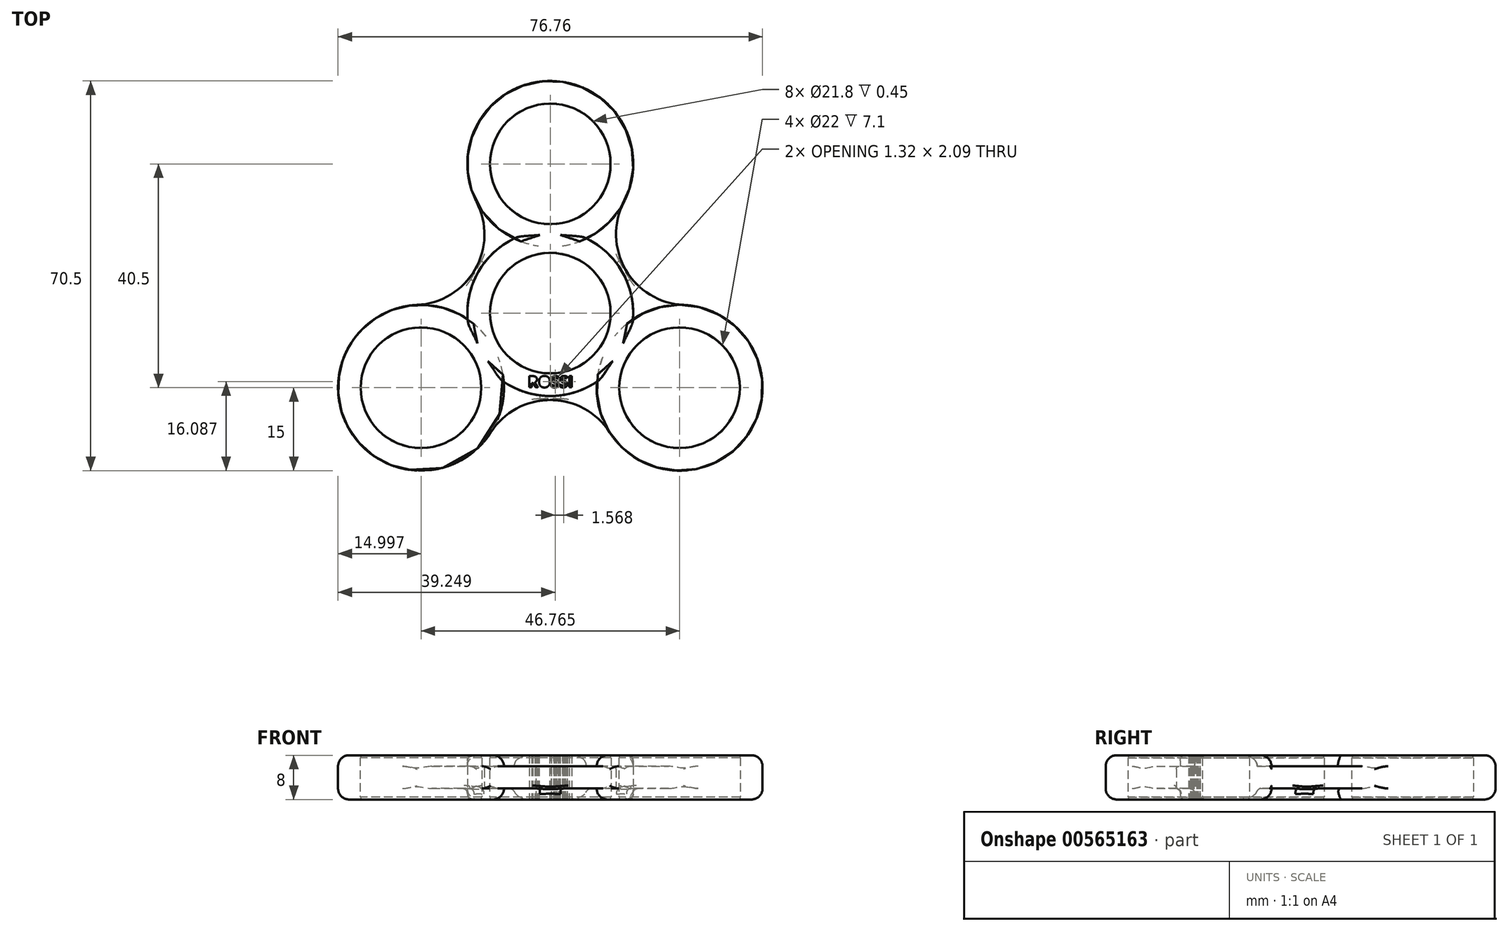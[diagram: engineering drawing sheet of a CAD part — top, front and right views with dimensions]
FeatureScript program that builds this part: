
annotation { "Feature Type Name" : "Feature", "Feature Type Description" : "" }
export const myFeature = defineFeature(function(context is Context, id is Id, definition is map)
    precondition{}
    {
        {
            var Q0;
            Q0=qCreatedBy(makeId("Top.planeOp"),FACE);
            var sketch = newSketch(context, id + "F0", { "sketchPlane" : qUnion([Q0])});
            skCircle(sketch, "E0", {"center": v(0, 0) * mm, "radius": 10.9 * mm});
            skCircle(sketch, "E1", {"center": v(0, 27) * mm, "radius": 10.9 * mm});
            skCircle(sketch, "E2.1.0", {"center": v(-23.38, -13.5) * mm, "radius": 10.9 * mm});
            skCircle(sketch, "E2.2.0", {"center": v(23.38, -13.5) * mm, "radius": 10.9 * mm});
            skArc(sketch, "E3", {"start": v(6.54, 13.5) * mm, "mid": v(0, 42) * mm, "end": v(-6.54, 13.5) * mm});
            skArc(sketch, "E4.1.0", {"start": v(8.42, -12.41) * mm, "mid": v(36.37, -21) * mm, "end": v(14.96, -1.09) * mm});
            skArc(sketch, "E4.2.0", {"start": v(-14.96, -1.09) * mm, "mid": v(-36.37, -21) * mm, "end": v(-8.42, -12.41) * mm});
            skArc(sketch, "E5", {"start": v(-8.42, -12.41) * mm, "mid": v(0, -15) * mm, "end": v(8.42, -12.41) * mm});
            skArc(sketch, "E6", {"start": v(-24.08, 1.48) * mm, "mid": v(-13.61, 7.86) * mm, "end": v(-13.33, 20.12) * mm});
            skArc(sketch, "E7", {"start": v(10.76, -21.6) * mm, "mid": v(0, -15.72) * mm, "end": v(-10.76, -21.6) * mm});
            skArc(sketch, "E8", {"start": v(13.33, 20.12) * mm, "mid": v(13.61, 7.86) * mm, "end": v(24.08, 1.48) * mm});
            skPoint(sketch, "E9.orphan", {"position": v(-13, 34.5) * mm});
            skPoint(sketch, "E10.orphan", {"position": v(-36.37, -6) * mm});
            skPoint(sketch, "E11.orphan", {"position": v(13, 34.5) * mm});
            skPoint(sketch, "E12.2.0.start.orphan", {"position": v(36.37, -6) * mm});
            skPoint(sketch, "E13.orphan", {"position": v(23.38, -28.5) * mm});
            skPoint(sketch, "E12.1.0.start.orphan", {"position": v(-23.38, -28.5) * mm});
            skArc(sketch, "E14.trimOffspring", {"start": v(14.96, -1.09) * mm, "mid": v(13, 7.5) * mm, "end": v(6.54, 13.5) * mm});
            skArc(sketch, "E15.trimOffspring", {"start": v(-6.54, 13.5) * mm, "mid": v(-13, 7.5) * mm, "end": v(-14.96, -1.09) * mm});
            skText(sketch, "E16", { "text": "ROSSI", "fontName": "OpenSans-Bold.ttf"});
            skCircle(sketch, "E17", {"center": v(23.38, -13.5) * mm, "radius": 11 * mm});
            skCircle(sketch, "E18", {"center": v(-23.38, -13.5) * mm, "radius": 11 * mm});
            skCircle(sketch, "E19", {"center": v(0, 0) * mm, "radius": 11 * mm});
            skCircle(sketch, "E20", {"center": v(0, 27) * mm, "radius": 11 * mm});
            const initialGuessF0  = {"E16": [-0.00407, -0.01343, 1, 0, 0.00205]};
            skSetInitialGuess(sketch, initialGuessF0);
            skSolve(sketch);
        }
        {
            var Q0;
            Q0=makeQuery(id+"F0.imprint","IMPRINT",FACE,{"disambiguationData":[TD([[makeQuery(id+"F0.imprint","IMPRINT",EDGE,{"derivedFrom":sQuery(id+"F0.wireOp",EDGE,"E2.1.0")}),-1.0]])]});
            var Q1;
            Q1=makeQuery(id+"F0.imprint","IMPRINT",FACE,{"disambiguationData":[TD([[makeQuery(id+"F0.imprint","IMPRINT",EDGE,{"derivedFrom":sQuery(id+"F0.wireOp",EDGE,"E0")}),-1.0]])]});
            var Q2;
            Q2=makeQuery(id+"F0.imprint","IMPRINT",FACE,{"disambiguationData":[TD([[makeQuery(id+"F0.imprint","IMPRINT",EDGE,{"derivedFrom":sQuery(id+"F0.wireOp",EDGE,"E1")}),-1.0]])]});
            var Q3;
            {var subQ0=sQuery(id+"F0.wireOp",EDGE,"E3");var subQ1=sQuery(id+"F0.wireOp",EDGE,"KJlQqC9l-gusD-toYh-YzLE-zyJcLNbmcpUm");var subQ2=makeQuery(id+"F0.imprint","INTERSECT",VERTEX,{"derivedFrom":[subQ1,subQ0]});Q3=makeQuery(id+"F0.imprint","IMPRINT",FACE,{"disambiguationData":[TD([[makeQuery(id+"F0.imprint","IMPRINT",EDGE,{"disambiguationData":[TD([[subQ2,1.0]])],"derivedFrom":subQ1}),1.0]])]});}
            var Q4;
            {var subQ0=sQuery(id+"F0.wireOp",EDGE,"E3");var subQ1=sQuery(id+"F0.wireOp",EDGE,"KJlQqC9l-gusD-toYh-YzLE-zyJcLNbmcpUm");var subQ2=makeQuery(id+"F0.imprint","INTERSECT",VERTEX,{"derivedFrom":[subQ1,subQ0]});Q4=makeQuery(id+"F0.imprint","IMPRINT",FACE,{"disambiguationData":[TD([[makeQuery(id+"F0.imprint","IMPRINT",EDGE,{"disambiguationData":[TD([[subQ2,1.0]])],"derivedFrom":subQ1}),-1.0]])]});}
            var Q5;
            {var subQ0=sQuery(id+"F0.wireOp",EDGE,"E5");var subQ1=sQuery(id+"F0.wireOp",EDGE,"E4.2.0");var subQ2=makeQuery(id+"F0.imprint","INTERSECT",VERTEX,{"disambiguationData":[OD(0.0)],"derivedFrom":[subQ1,subQ0]});Q5=makeQuery(id+"F0.imprint","IMPRINT",FACE,{"disambiguationData":[TD([[makeQuery(id+"F0.imprint","IMPRINT",EDGE,{"disambiguationData":[TD([[subQ2,-1.0]])],"derivedFrom":subQ1}),1.0]])]});}
            var Q6;
            Q6=makeQuery(id+"F0.imprint","IMPRINT",FACE,{"disambiguationData":[TD([[makeQuery(id+"F0.imprint","IMPRINT",EDGE,{"derivedFrom":sQuery(id+"F0.wireOp",EDGE,"E2.2.0")}),-1.0]])]});
            var Q7;
            {var subQ0=sQuery(id+"F0.wireOp",EDGE,"E5");var subQ1=sQuery(id+"F0.wireOp",EDGE,"E4.1.0");var subQ2=makeQuery(id+"F0.imprint","INTERSECT",VERTEX,{"disambiguationData":[OD(0.0)],"derivedFrom":[subQ1,subQ0]});Q7=makeQuery(id+"F0.imprint","IMPRINT",FACE,{"disambiguationData":[TD([[makeQuery(id+"F0.imprint","IMPRINT",EDGE,{"disambiguationData":[TD([[subQ2,-1.0]])],"derivedFrom":subQ1}),1.0]])]});}
            extrude(context, id + "F1", {"entities" : qUnion([Q0, Q1, Q2, Q3, Q4, Q5, Q6, Q7]), "endBound" : BoundingType.SYMMETRIC, "depth" : 8 * mm, "offsetDistance" : 25 * mm});
        }
        {
            var Q0;
            {var subQ0=sQuery(id+"F0.wireOp",EDGE,"E7");Q0=makeQuery(id+"F0.imprint","IMPRINT",FACE,{"disambiguationData":[TD([[makeQuery(id+"F0.imprint","IMPRINT",EDGE,{"derivedFrom":subQ0}),-1.0]])]});}
            var Q1;
            {var subQ0=sQuery(id+"F0.wireOp",EDGE,"E6");Q1=makeQuery(id+"F0.imprint","IMPRINT",FACE,{"disambiguationData":[TD([[makeQuery(id+"F0.imprint","IMPRINT",EDGE,{"derivedFrom":subQ0}),-1.0]])]});}
            var Q2;
            {var subQ0=sQuery(id+"F0.wireOp",EDGE,"E8");Q2=makeQuery(id+"F0.imprint","IMPRINT",FACE,{"disambiguationData":[TD([[makeQuery(id+"F0.imprint","IMPRINT",EDGE,{"derivedFrom":subQ0}),-1.0]])]});}
            extrude(context, id + "F2", {"entities" : qUnion([Q0, Q1, Q2]), "operationType" : NewBodyOperationType.ADD, "endBound" : BoundingType.SYMMETRIC, "depth" : 4 * mm, "offsetDistance" : 25 * mm});
        }
        {
            var Q0;
            Q0=makeQuery(id+"F1.opExtrude","CAP_EDGE",EDGE,{"disambiguationData":[OSD([sQuery(id+"F0.wireOp",EDGE,"E15.trimOffspring")])],"isStart":true});
            var Q1;
            Q1=makeQuery(id+"F2.opExtrude","CAP_EDGE",EDGE,{"disambiguationData":[OSD([sQuery(id+"F0.wireOp",EDGE,"E15.trimOffspring")])],"isStart":true});
            var Q2;
            Q2=makeQuery(id+"F1.opExtrude","CAP_EDGE",EDGE,{"disambiguationData":[OSD([sQuery(id+"F0.wireOp",EDGE,"E5")])],"isStart":true});
            var Q3;
            Q3=makeQuery(id+"F2.opExtrude","CAP_EDGE",EDGE,{"disambiguationData":[OSD([sQuery(id+"F0.wireOp",EDGE,"E5")])],"isStart":true});
            var Q4;
            Q4=makeQuery(id+"F1.opExtrude","CAP_EDGE",EDGE,{"disambiguationData":[OSD([sQuery(id+"F0.wireOp",EDGE,"E14.trimOffspring")])],"isStart":true});
            var Q5;
            Q5=makeQuery(id+"F2.opExtrude","CAP_EDGE",EDGE,{"disambiguationData":[OSD([sQuery(id+"F0.wireOp",EDGE,"E14.trimOffspring")])],"isStart":true});
            fillet(context, id + "F3", {"entities" : qUnion([Q0, Q1, Q2, Q3, Q4, Q5]), "radius" : 1 * mm, "rho" : 0.5, "crossSection" : FilletCrossSection.CONIC, "allowEdgeOverflow" : false});
        }
        {
            var Q0;
            Q0=makeQuery(id+"F1.opExtrude","CAP_EDGE",EDGE,{"disambiguationData":[OSD([sQuery(id+"F0.wireOp",EDGE,"E5")])],"isStart":false});
            var Q1;
            Q1=makeQuery(id+"F2.opExtrude","CAP_EDGE",EDGE,{"disambiguationData":[OSD([sQuery(id+"F0.wireOp",EDGE,"E5")])],"isStart":false});
            var Q2;
            Q2=makeQuery(id+"F1.opExtrude","CAP_EDGE",EDGE,{"disambiguationData":[OSD([sQuery(id+"F0.wireOp",EDGE,"E14.trimOffspring")])],"isStart":false});
            var Q3;
            Q3=makeQuery(id+"F2.opExtrude","CAP_EDGE",EDGE,{"disambiguationData":[OSD([sQuery(id+"F0.wireOp",EDGE,"E14.trimOffspring")])],"isStart":false});
            var Q4;
            Q4=makeQuery(id+"F1.opExtrude","CAP_EDGE",EDGE,{"disambiguationData":[OSD([sQuery(id+"F0.wireOp",EDGE,"E15.trimOffspring")])],"isStart":false});
            var Q5;
            Q5=makeQuery(id+"F2.opExtrude","CAP_EDGE",EDGE,{"disambiguationData":[OSD([sQuery(id+"F0.wireOp",EDGE,"E15.trimOffspring")])],"isStart":false});
            fillet(context, id + "F4", {"entities" : qUnion([Q0, Q1, Q2, Q3, Q4, Q5]), "radius" : 1 * mm, "rho" : 0.5, "crossSection" : FilletCrossSection.CONIC, "allowEdgeOverflow" : false});
        }
        {
            var Q0;
            Q0=makeQuery(id+"F1.opExtrude","CAP_EDGE",EDGE,{"disambiguationData":[OSD([sQuery(id+"F0.wireOp",EDGE,"E4.1.0")])],"isStart":false});
            var Q1;
            Q1=makeQuery(id+"F1.opExtrude","CAP_EDGE",EDGE,{"disambiguationData":[OSD([sQuery(id+"F0.wireOp",EDGE,"E3")])],"isStart":false});
            var Q2;
            Q2=makeQuery(id+"F1.opExtrude","CAP_EDGE",EDGE,{"disambiguationData":[OSD([sQuery(id+"F0.wireOp",EDGE,"E4.2.0")])],"isStart":false});
            var Q3;
            Q3=makeQuery(id+"F1.opExtrude","CAP_EDGE",EDGE,{"disambiguationData":[OSD([sQuery(id+"F0.wireOp",EDGE,"E4.2.0")])],"isStart":true});
            var Q4;
            Q4=makeQuery(id+"F1.opExtrude","CAP_EDGE",EDGE,{"disambiguationData":[OSD([sQuery(id+"F0.wireOp",EDGE,"E4.1.0")])],"isStart":true});
            var Q5;
            Q5=makeQuery(id+"F1.opExtrude","CAP_EDGE",EDGE,{"disambiguationData":[OSD([sQuery(id+"F0.wireOp",EDGE,"E3")])],"isStart":true});
            fillet(context, id + "F5", {"entities" : qUnion([Q0, Q1, Q2, Q3, Q4, Q5]), "radius" : 2 * mm, "allowEdgeOverflow" : false});
        }
        {
            var Q0;
            Q0=makeQuery(id+"F2.opExtrude","SWEPT_FACE",FACE,{"disambiguationData":[OSD([sQuery(id+"F0.wireOp",EDGE,"E8")])]});
            var Q1;
            Q1=makeQuery(id+"F2.opExtrude","SWEPT_FACE",FACE,{"disambiguationData":[OSD([sQuery(id+"F0.wireOp",EDGE,"E6")])]});
            var Q2;
            Q2=makeQuery(id+"F2.opExtrude","SWEPT_FACE",FACE,{"disambiguationData":[OSD([sQuery(id+"F0.wireOp",EDGE,"E7")])]});
            fillet(context, id + "F6", {"entities" : qUnion([Q0, Q1, Q2]), "radius" : .5 * mm, "tangentPropagation" : true, "allowEdgeOverflow" : false});
        }
        {
            var Q0;
            Q0=makeQuery(id+"F0.imprint","IMPRINT",FACE,{"disambiguationData":[TD([[makeQuery(id+"F0.imprint","IMPRINT",EDGE,{"derivedFrom":sQuery(id+"F0.wireOp",EDGE,"E20")}),1.0]])]});
            var Q1;
            Q1=makeQuery(id+"F0.imprint","IMPRINT",FACE,{"disambiguationData":[TD([[makeQuery(id+"F0.imprint","IMPRINT",EDGE,{"derivedFrom":sQuery(id+"F0.wireOp",EDGE,"E19")}),1.0]])]});
            var Q2;
            Q2=makeQuery(id+"F0.imprint","IMPRINT",FACE,{"disambiguationData":[TD([[makeQuery(id+"F0.imprint","IMPRINT",EDGE,{"derivedFrom":sQuery(id+"F0.wireOp",EDGE,"E17")}),1.0]])]});
            var Q3;
            Q3=makeQuery(id+"F0.imprint","IMPRINT",FACE,{"disambiguationData":[TD([[makeQuery(id+"F0.imprint","IMPRINT",EDGE,{"derivedFrom":sQuery(id+"F0.wireOp",EDGE,"E18")}),1.0]])]});
            extrude(context, id + "F7", {"entities" : qUnion([Q0, Q1, Q2, Q3]), "endBound" : BoundingType.SYMMETRIC, "depth" : 7.1 * mm, "offsetDistance" : 25 * mm});
        }
        {
            var Q0;
            Q0=makeQuery(id+"F7.opExtrude","SWEPT_BODY",BODY,{"disambiguationData":[OSD([sQuery(id+"F0.wireOp",EDGE,"E17")])]});
            var Q1;
            Q1=makeQuery(id+"F7.opExtrude","SWEPT_BODY",BODY,{"disambiguationData":[OSD([sQuery(id+"F0.wireOp",EDGE,"E18")])]});
            var Q2;
            Q2=makeQuery(id+"F7.opExtrude","SWEPT_BODY",BODY,{"disambiguationData":[OSD([sQuery(id+"F0.wireOp",EDGE,"E19")])]});
            var Q3;
            Q3=makeQuery(id+"F7.opExtrude","SWEPT_BODY",BODY,{"disambiguationData":[OSD([sQuery(id+"F0.wireOp",EDGE,"E20")])]});
            var Q4;
            Q4=makeQuery(id+"F1.opExtrude","SWEPT_BODY",BODY,{"disambiguationData":[OSD([sQuery(id+"F0.wireOp",EDGE,"E0"),sQuery(id+"F0.wireOp",EDGE,"E1"),sQuery(id+"F0.wireOp",EDGE,"E2.1.0"),sQuery(id+"F0.wireOp",EDGE,"E2.2.0"),sQuery(id+"F0.wireOp",EDGE,"E3"),sQuery(id+"F0.wireOp",EDGE,"E4.1.0"),sQuery(id+"F0.wireOp",EDGE,"E4.2.0"),sQuery(id+"F0.wireOp",EDGE,"E5"),sQuery(id+"F0.wireOp",EDGE,"E14.trimOffspring"),sQuery(id+"F0.wireOp",EDGE,"E15.trimOffspring"),sQuery(id+"F0.wireOp",EDGE,"E16.sketch_text.stroke-7"),sQuery(id+"F0.wireOp",EDGE,"E16.sketch_text.stroke-8"),sQuery(id+"F0.wireOp",EDGE,"E16.sketch_text.stroke-9"),sQuery(id+"F0.wireOp",EDGE,"E16.sketch_text.stroke-10"),sQuery(id+"F0.wireOp",EDGE,"E16.sketch_text.stroke-11"),sQuery(id+"F0.wireOp",EDGE,"E16.sketch_text.stroke-12"),sQuery(id+"F0.wireOp",EDGE,"E16.sketch_text.stroke-13"),sQuery(id+"F0.wireOp",EDGE,"E16.sketch_text.stroke-14"),sQuery(id+"F0.wireOp",EDGE,"E16.sketch_text.stroke-15"),sQuery(id+"F0.wireOp",EDGE,"E16.sketch_text.stroke-16"),sQuery(id+"F0.wireOp",EDGE,"E16.sketch_text.stroke-17"),sQuery(id+"F0.wireOp",EDGE,"E16.sketch_text.stroke-18"),sQuery(id+"F0.wireOp",EDGE,"E16.sketch_text.stroke-19"),sQuery(id+"F0.wireOp",EDGE,"E16.sketch_text.stroke-20"),sQuery(id+"F0.wireOp",EDGE,"E16.sketch_text.stroke-21"),sQuery(id+"F0.wireOp",EDGE,"E16.sketch_text.stroke-22"),sQuery(id+"F0.wireOp",EDGE,"E16.sketch_text.stroke-23"),sQuery(id+"F0.wireOp",EDGE,"E16.sketch_text.stroke-28"),sQuery(id+"F0.wireOp",EDGE,"E16.sketch_text.stroke-29"),sQuery(id+"F0.wireOp",EDGE,"E16.sketch_text.stroke-30"),sQuery(id+"F0.wireOp",EDGE,"E16.sketch_text.stroke-31"),sQuery(id+"F0.wireOp",EDGE,"E16.sketch_text.stroke-32"),sQuery(id+"F0.wireOp",EDGE,"E16.sketch_text.stroke-33"),sQuery(id+"F0.wireOp",EDGE,"E16.sketch_text.stroke-34"),sQuery(id+"F0.wireOp",EDGE,"E16.sketch_text.stroke-35"),sQuery(id+"F0.wireOp",EDGE,"E16.sketch_text.stroke-36"),sQuery(id+"F0.wireOp",EDGE,"E16.sketch_text.stroke-37"),sQuery(id+"F0.wireOp",EDGE,"E16.sketch_text.stroke-38"),sQuery(id+"F0.wireOp",EDGE,"E16.sketch_text.stroke-39"),sQuery(id+"F0.wireOp",EDGE,"E16.sketch_text.stroke-40"),sQuery(id+"F0.wireOp",EDGE,"E16.sketch_text.stroke-41"),sQuery(id+"F0.wireOp",EDGE,"E16.sketch_text.stroke-42"),sQuery(id+"F0.wireOp",EDGE,"E16.sketch_text.stroke-43"),sQuery(id+"F0.wireOp",EDGE,"E16.sketch_text.stroke-44"),sQuery(id+"F0.wireOp",EDGE,"E16.sketch_text.stroke-45"),sQuery(id+"F0.wireOp",EDGE,"E16.sketch_text.stroke-46"),sQuery(id+"F0.wireOp",EDGE,"E16.sketch_text.stroke-47"),sQuery(id+"F0.wireOp",EDGE,"E16.sketch_text.stroke-48"),sQuery(id+"F0.wireOp",EDGE,"E16.sketch_text.stroke-49"),sQuery(id+"F0.wireOp",EDGE,"E16.sketch_text.stroke-50"),sQuery(id+"F0.wireOp",EDGE,"E16.sketch_text.stroke-51"),sQuery(id+"F0.wireOp",EDGE,"E16.sketch_text.stroke-52"),sQuery(id+"F0.wireOp",EDGE,"E16.sketch_text.stroke-53"),sQuery(id+"F0.wireOp",EDGE,"E16.sketch_text.stroke-54"),sQuery(id+"F0.wireOp",EDGE,"E16.sketch_text.stroke-55"),sQuery(id+"F0.wireOp",EDGE,"E16.sketch_text.stroke-56"),sQuery(id+"F0.wireOp",EDGE,"E16.sketch_text.stroke-57"),sQuery(id+"F0.wireOp",EDGE,"E16.sketch_text.stroke-58"),sQuery(id+"F0.wireOp",EDGE,"E16.sketch_text.stroke-59"),sQuery(id+"F0.wireOp",EDGE,"E16.sketch_text.stroke-60"),sQuery(id+"F0.wireOp",EDGE,"E16.sketch_text.stroke-74"),sQuery(id+"F0.wireOp",EDGE,"E16.sketch_text.stroke-75"),sQuery(id+"F0.wireOp",EDGE,"E16.sketch_text.stroke-76"),sQuery(id+"F0.wireOp",EDGE,"E16.sketch_text.stroke-77"),sQuery(id+"F0.wireOp",EDGE,"E16.sketch_text.stroke-78"),sQuery(id+"F0.wireOp",EDGE,"E16.sketch_text.stroke-79"),sQuery(id+"F0.wireOp",EDGE,"E16.sketch_text.stroke-80"),sQuery(id+"F0.wireOp",EDGE,"E16.sketch_text.stroke-81"),sQuery(id+"F0.wireOp",EDGE,"E16.sketch_text.stroke-86"),sQuery(id+"F0.wireOp",EDGE,"E16.sketch_text.stroke-87"),sQuery(id+"F0.wireOp",EDGE,"E16.sketch_text.stroke-88"),sQuery(id+"F0.wireOp",EDGE,"E16.sketch_text.stroke-89"),sQuery(id+"F0.wireOp",EDGE,"E16.sketch_text.stroke-90"),sQuery(id+"F0.wireOp",EDGE,"E16.sketch_text.stroke-91"),sQuery(id+"F0.wireOp",EDGE,"E16.sketch_text.stroke-92"),sQuery(id+"F0.wireOp",EDGE,"E16.sketch_text.stroke-93"),sQuery(id+"F0.wireOp",EDGE,"E16.sketch_text.stroke-94"),sQuery(id+"F0.wireOp",EDGE,"E16.sketch_text.stroke-95"),sQuery(id+"F0.wireOp",EDGE,"E16.sketch_text.stroke-96"),sQuery(id+"F0.wireOp",EDGE,"E16.sketch_text.stroke-97"),sQuery(id+"F0.wireOp",EDGE,"E16.sketch_text.stroke-98"),sQuery(id+"F0.wireOp",EDGE,"E16.sketch_text.stroke-99"),sQuery(id+"F0.wireOp",EDGE,"E16.sketch_text.stroke-100"),sQuery(id+"F0.wireOp",EDGE,"E16.sketch_text.stroke-101"),sQuery(id+"F0.wireOp",EDGE,"E16.sketch_text.stroke-102"),sQuery(id+"F0.wireOp",EDGE,"E16.sketch_text.stroke-103"),sQuery(id+"F0.wireOp",EDGE,"E16.sketch_text.stroke-104"),sQuery(id+"F0.wireOp",EDGE,"E16.sketch_text.stroke-105"),sQuery(id+"F0.wireOp",EDGE,"E16.sketch_text.stroke-106"),sQuery(id+"F0.wireOp",EDGE,"E16.sketch_text.stroke-107"),sQuery(id+"F0.wireOp",EDGE,"E16.sketch_text.stroke-108"),sQuery(id+"F0.wireOp",EDGE,"E16.sketch_text.stroke-109"),sQuery(id+"F0.wireOp",EDGE,"E16.sketch_text.stroke-110"),sQuery(id+"F0.wireOp",EDGE,"E16.sketch_text.stroke-111"),sQuery(id+"F0.wireOp",EDGE,"E16.sketch_text.stroke-112"),sQuery(id+"F0.wireOp",EDGE,"E16.sketch_text.stroke-113"),sQuery(id+"F0.wireOp",EDGE,"E16.sketch_text.stroke-114"),sQuery(id+"F0.wireOp",EDGE,"E16.sketch_text.stroke-115"),sQuery(id+"F0.wireOp",EDGE,"E16.sketch_text.stroke-116"),sQuery(id+"F0.wireOp",EDGE,"E16.sketch_text.stroke-117"),sQuery(id+"F0.wireOp",EDGE,"E16.sketch_text.stroke-118"),sQuery(id+"F0.wireOp",EDGE,"E16.sketch_text.stroke-119"),sQuery(id+"F0.wireOp",EDGE,"E16.sketch_text.stroke-120"),sQuery(id+"F0.wireOp",EDGE,"E16.sketch_text.stroke-121"),sQuery(id+"F0.wireOp",EDGE,"E16.sketch_text.stroke-122"),sQuery(id+"F0.wireOp",EDGE,"E16.sketch_text.stroke-123"),sQuery(id+"F0.wireOp",EDGE,"E16.sketch_text.stroke-124"),sQuery(id+"F0.wireOp",EDGE,"E16.sketch_text.stroke-125"),sQuery(id+"F0.wireOp",EDGE,"E16.sketch_text.stroke-126"),sQuery(id+"F0.wireOp",EDGE,"E16.sketch_text.stroke-127"),sQuery(id+"F0.wireOp",EDGE,"E16.sketch_text.stroke-128"),sQuery(id+"F0.wireOp",EDGE,"E16.sketch_text.stroke-129"),sQuery(id+"F0.wireOp",EDGE,"E16.sketch_text.stroke-130"),sQuery(id+"F0.wireOp",EDGE,"E16.sketch_text.stroke-131"),sQuery(id+"F0.wireOp",EDGE,"E16.sketch_text.stroke-132"),sQuery(id+"F0.wireOp",EDGE,"E16.sketch_text.stroke-133"),sQuery(id+"F0.wireOp",EDGE,"E16.sketch_text.stroke-134"),sQuery(id+"F0.wireOp",EDGE,"E16.sketch_text.stroke-135"),sQuery(id+"F0.wireOp",EDGE,"E16.sketch_text.stroke-136"),sQuery(id+"F0.wireOp",EDGE,"E16.sketch_text.stroke-137"),sQuery(id+"F0.wireOp",EDGE,"E16.sketch_text.stroke-138"),sQuery(id+"F0.wireOp",EDGE,"E16.sketch_text.stroke-139"),sQuery(id+"F0.wireOp",EDGE,"E16.sketch_text.stroke-140"),sQuery(id+"F0.wireOp",EDGE,"E16.sketch_text.stroke-141"),sQuery(id+"F0.wireOp",EDGE,"E16.sketch_text.stroke-142"),sQuery(id+"F0.wireOp",EDGE,"E16.sketch_text.stroke-143"),sQuery(id+"F0.wireOp",EDGE,"E16.sketch_text.stroke-144"),sQuery(id+"F0.wireOp",EDGE,"E16.sketch_text.stroke-145"),sQuery(id+"F0.wireOp",EDGE,"E16.sketch_text.stroke-146"),sQuery(id+"F0.wireOp",EDGE,"E16.sketch_text.stroke-147"),sQuery(id+"F0.wireOp",EDGE,"E16.sketch_text.stroke-148"),sQuery(id+"F0.wireOp",EDGE,"E16.sketch_text.stroke-149"),sQuery(id+"F0.wireOp",EDGE,"E16.sketch_text.stroke-150"),sQuery(id+"F0.wireOp",EDGE,"E16.sketch_text.stroke-151"),sQuery(id+"F0.wireOp",EDGE,"E16.sketch_text.stroke-152"),sQuery(id+"F0.wireOp",EDGE,"E16.sketch_text.stroke-153"),sQuery(id+"F0.wireOp",EDGE,"E16.sketch_text.stroke-154"),sQuery(id+"F0.wireOp",EDGE,"E16.sketch_text.stroke-155"),sQuery(id+"F0.wireOp",EDGE,"E16.sketch_text.stroke-156"),sQuery(id+"F0.wireOp",EDGE,"E16.sketch_text.stroke-157"),sQuery(id+"F0.wireOp",EDGE,"E16.sketch_text.stroke-158"),sQuery(id+"F0.wireOp",EDGE,"E16.sketch_text.stroke-159"),sQuery(id+"F0.wireOp",EDGE,"E16.sketch_text.stroke-160"),sQuery(id+"F0.wireOp",EDGE,"E16.sketch_text.stroke-161"),sQuery(id+"F0.wireOp",EDGE,"E16.sketch_text.stroke-162"),sQuery(id+"F0.wireOp",EDGE,"E16.sketch_text.stroke-163"),sQuery(id+"F0.wireOp",EDGE,"E16.sketch_text.stroke-164"),sQuery(id+"F0.wireOp",EDGE,"E16.sketch_text.stroke-165"),sQuery(id+"F0.wireOp",EDGE,"E16.sketch_text.stroke-166"),sQuery(id+"F0.wireOp",EDGE,"E16.sketch_text.stroke-167"),sQuery(id+"F0.wireOp",EDGE,"E16.sketch_text.stroke-168"),sQuery(id+"F0.wireOp",EDGE,"E16.sketch_text.stroke-169"),sQuery(id+"F0.wireOp",EDGE,"E16.sketch_text.stroke-170")])]});
            booleanBodies(context, id + "F8", {"operationType" : BooleanOperationType.SUBTRACTION, "tools" : qUnion([Q0, Q1, Q2, Q3]), "targets" : qUnion([Q4])});
        }
    });
